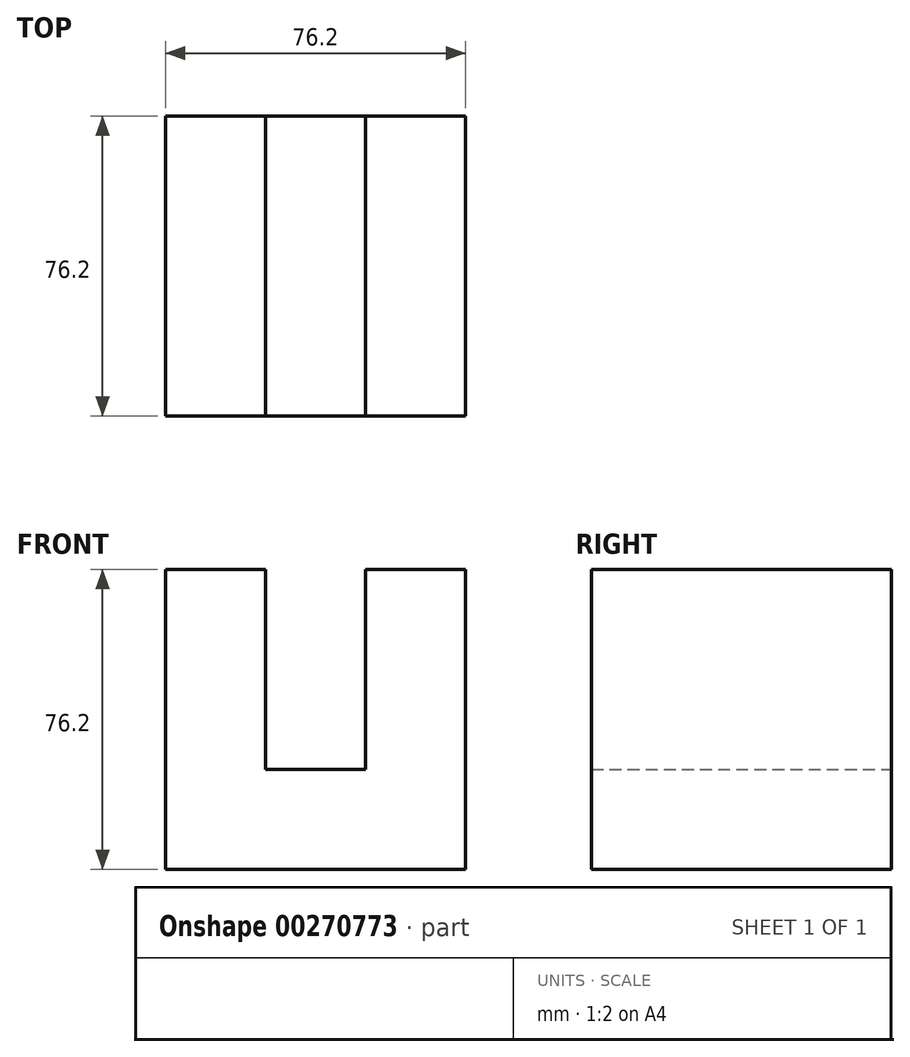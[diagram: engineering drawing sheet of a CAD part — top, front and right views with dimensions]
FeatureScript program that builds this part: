
annotation { "Feature Type Name" : "Feature", "Feature Type Description" : "" }
export const myFeature = defineFeature(function(context is Context, id is Id, definition is map)
    precondition{}
    {
        {
            var Q0;
            Q0=qCreatedBy(makeId("Front.planeOp"),FACE);
            var sketch = newSketch(context, id + "F0", { "sketchPlane" : qUnion([Q0])});
            skLineSegment(sketch, "E0", {"start": v(38.77, 0) * mm, "end": v(-37.43, 0) * mm});
            skLineSegment(sketch, "E1", {"start": v(-37.43, 0) * mm, "end": v(-37.43, 76.2) * mm});
            skLineSegment(sketch, "E2", {"start": v(-37.43, 76.2) * mm, "end": v(-12.03, 76.2) * mm});
            skLineSegment(sketch, "E3", {"start": v(-12.03, 76.2) * mm, "end": v(-12.03, 25.4) * mm});
            skLineSegment(sketch, "E4", {"start": v(-12.03, 25.4) * mm, "end": v(13.37, 25.4) * mm});
            skLineSegment(sketch, "E5", {"start": v(13.37, 25.4) * mm, "end": v(13.37, 76.2) * mm});
            skLineSegment(sketch, "E6", {"start": v(13.37, 76.2) * mm, "end": v(38.77, 76.2) * mm});
            skLineSegment(sketch, "E7", {"start": v(38.77, 76.2) * mm, "end": v(38.77, 0) * mm});
            skSolve(sketch);
        }
        {
            var Q0;
            Q0 = qSketchRegion(id + "F0", true);
            extrude(context, id + "F1", {"entities" : qUnion([Q0]), "depth" : 76.2 * mm});
        }
    });
